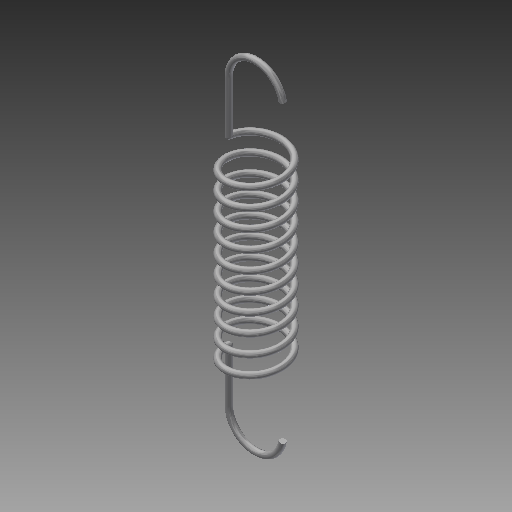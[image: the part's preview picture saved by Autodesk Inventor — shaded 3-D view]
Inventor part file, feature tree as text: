
AUTODESK INVENTOR PART (.ipt)
format: ipt  version: 2019 (Build 230136000, 136)  size: 1,031,168 bytes
history: native  units: mm
features: sketch x104, plane x32, other x32, extrude x10, sweep x6
ambient origin geometry x8: Origin, YZ Plane, XZ Plane, XY Plane, X Axis, Y Axis, Z Axis, Center Point
bodies: Solid1 (feature_tree)
feature tree (184):
  sketch  "Sketch1"  dims[d0=0.25mm d1=4.5mm]
  sketch  "3D Sketch2"
  plane  "Work PlaneSweep1"
  other  "First revolution with hook type 0(Right)"
  sketch  "Sketch8"  dims[d17=90.0deg d24=0.0mm d25=2.9972mm]
  plane  "Work PlaneExtrusion7"
  sketch  "Sketch10"  dims[d28=0.0mm d29=90.0deg d30=90.0deg d31=0.0mm d32=0.0mm d33=1.0mm]
  plane  "Work PlaneSweep2"
  sweep  "Sweep2"
  other  "Second revolution with hook type 0(Right)"
  sketch  "Sketch12"  dims[d38=90.0deg d54=10.0mm d55=10.0mm]
  plane  "Work PlaneExtrusion8"
  sketch  "Sketch110"  dims[d367=29.670597mm]
  sketch  "3D Sketch20"
  plane  "Work PlaneSweep3"
  sketch  "3D Sketch3"
  plane  "Work PlaneSweep6"
  other  "First revolution with hook type 0(Left)"
  sketch  "Sketch24"  dims[d180=90.0deg]
  plane  "Work PlaneExtrusion5"
  sketch  "Sketch18"  dims[d169=300.0deg d170=6.257mm]
  plane  "Work PlaneSweep7"
  sweep  "Sweep7"
  other  "Second revolution with hook type 0(Left)"
  sketch  "Sketch20"  dims[d173=300.0deg d174=6.257mm]
  plane  "Work PlaneExtrusion6"
  sketch  "Sketch22"  dims[d177=6.507mm d178=0.0mm]
  plane  "Work PlaneSweep8"
  other  "First revolution with hook type 1(Left)"
  sketch  "Sketch27"  dims[d182=6.507mm]
  plane  "Work PlaneExtrusion9"
  extrude  "Extrusion9"  TaperAngle=90.0deg  [1 undecoded]
  sketch  "Sketch29"  dims[d184=30.0mm d185=30.0mm d186=30.0mm]
  plane  "Work PlaneSweep9"
  other  "Second revolution with hook type 1(Left)"
  sketch  "Sketch32"  dims[d189=4.5mm]
  plane  "Work PlaneExtrusion10"
  sketch  "Sketch34"  dims[d191=300.0deg]
  sketch  "3D Sketch22"
  plane  "Work PlaneSweep10"
  other  "First revolution with hook type 1(Right)"
  sketch  "Sketch42"  dims[d195=40.0mm]
  plane  "Work PlaneExtrusion11"
  extrude  "Extrusion11"  Depth=2.9972mm TaperAngle=0.0deg
  sketch  "Sketch44"  dims[d197=0.0mm]
  plane  "Work PlaneSweep11"
  other  "Second revolution with hook type 1(Right)"
  sketch  "Sketch112"  dims[d373=20.0mm]
  plane  "Work PlaneExtrusion12"
  sketch  "Sketch114"  dims[d375=0.0mm]
  sketch  "3D Sketch24"
  plane  "Work PlaneSweep12"
  sketch  "Sketch46"  dims[d199=300.0deg]
  other  "First sweep with hook type 2(Left)"
  sweep  "SweepLeftHook21"
  sketch  "Sketch48"  dims[d200=6.257mm]
  other  "Second sweep with hook type 2(Left)"
  sweep  "SweepLeftHook22"
  sketch  "Sketch50"  dims[d201=0.0mm]
  other  "First sweep with hook type 2(Right)"
  sweep  "SweepRightHook21"
  sketch  "Sketch52"  dims[d202=90.0deg]
  other  "Second sweep with hook type 2(Right)"
  sweep  "SweepRightHook22"
  other  "First revolution with hook type 3(Left)"
  extrude  "Extrusion1"  Depth=20.0mm
  other  "Second revolution with hook type 3(Left)"
  extrude  "Extrusion2"  Depth=20.0mm
  sketch  "Sketch60"  dims[d209=90.0deg]
  plane  "Work PlaneSweep20"
  other  "First revolution with hook type 3(Right)"
  extrude  "Extrusion3"  Depth=20.0mm
  other  "Second revolution with hook type 3(Right)"
  extrude  "Extrusion4"  Depth=6.257mm
  sketch  "Sketch68"  dims[d216=40.0mm]
  plane  "Work Plane46"
  other  "First revolution with hook type 4(Left)"
  sketch  "Sketch71"  dims[d223=90.0deg]
  plane  "Work PlaneExtrusion13"
  extrude  "Extrusion13"  TaperAngle=90.0deg  [1 undecoded]
  sketch  "Sketch73"  dims[d229=90.0deg]
  plane  "Work PlaneSweep23"
  other  "Second revolution with hook type 4(Left)"
  sketch  "Sketch76"  dims[d238=50.0mm]
  plane  "Work PlaneExtrusion14"
  sketch  "Sketch78"  dims[d243=60.0mm]
  sketch  "3D Sketch26"
  plane  "Work PlaneSweep24"
  other  "First revolution with hook type 4(Right)"
  sketch  "Sketch86"  dims[d269=60.0mm]
  plane  "Work PlaneExtrusion15"
  extrude  "Extrusion15"  Depth=6.257mm
  sketch  "Sketch88"  dims[d282=60.0mm]
  plane  "Work PlaneSweep25"
  other  "Second revolution with hook type 4(Right)"
  sketch  "Sketch116"  dims[d377=210.0deg]
  plane  "Work PlaneExtrusion16"
  sketch  "Sketch118"  dims[d381=20.0mm]
  sketch  "3D Sketch28"
  plane  "Work PlaneSweep26"
  other  "First revolution with hook type 5(Left)"
  sketch  "Sketch91"  dims[d301=10.0mm d302=15.0mm d303=0.0mm d304=90.0deg d305=90.0deg d306=0.0mm d307=0.0mm]
  plane  "Work PlaneExtrusion17"
  extrude  "Extrusion17"  TaperAngle=300.0deg  [1 undecoded]
  other  "Second revolution with hook type 5(Left)"
  sketch  "Sketch95"  dims[d320=6.507mm]
  plane  "Work PlaneExtrusion18"
  other  "First revolution with hook type 5(Right)"
  sketch  "Sketch99"  dims[d331=1.5mm]
  plane  "Work PlaneExtrusion19"
  other  "Second revolution with hook type 5(Right)"
  sketch  "Sketch103"  dims[d364=8.514mm]
  plane  "Work PlaneExtrusion20"
  extrude  "Extrusion20"  TaperAngle=0.0deg  [1 undecoded]
  sketch  "Sketch105"  dims[d366=10.0mm]
  other  "First coil with hook type 6(Left)"
  other  "Second coil with hook type 6(Left)"
  other  "First coil with hook type 6(Right)"
  other  "Second coil with hook type 6(Right)"
  other  "Srf1"
  sketch  "Sketch3"  dims[d2=2.9972mm d3=10.0mm d4=100.0mm]
  sketch  "Sketch4"  dims[d5=0.0mm d6=90.0deg d7=90.0deg d8=0.0mm d9=0.0mm d12=1.0mm]
  sketch  "Sketch7"  dims[d13=0.0mm d14=90.0deg]
  other  "Srf2"
  sketch  "3D Sketch14"
  sketch  "Sketch16"  dims[d149=90.0deg d152=20.0mm]
  sketch  "Sketch26"  dims[d181=300.0deg]
  sketch  "Sketch31"  dims[d188=40.0mm]
  sketch  "Sketch36"  dims[d193=0.0mm]
  sketch  "Sketch41"  dims[d194=90.0deg]
  sketch  "Sketch54"  dims[d203=40.0mm]
  sketch  "Sketch55"  dims[d204=4.5mm d205=0.0mm]
  sketch  "Sketch56"  dims[d206=300.0deg]
  sketch  "Sketch58"  dims[d207=6.257mm]
  sketch  "Sketch59"  dims[d208=0.0mm]
  sketch  "Sketch61"  dims[d210=4.5mm]
  sketch  "Sketch62"  dims[d211=0.0mm]
  sketch  "Sketch63"  dims[d212=90.0deg]
  sketch  "Sketch64"  dims[d213=300.0deg]
  sketch  "Sketch66"  dims[d214=6.257mm]
  sketch  "Sketch67"  dims[d215=0.0mm]
  sketch  "Sketch69"  dims[d217=90.0deg]
  sketch  "Sketch70"  dims[d220=50.0mm]
  sketch  "Sketch75"  dims[d235=90.0deg]
  sketch  "Sketch80"  dims[d256=60.0mm]
  sketch  "Sketch85"  dims[d268=90.0deg]
  sketch  "Sketch90"  dims[d300=1.5mm]
  sketch  "Sketch94"  dims[d311=10.0mm d312=15.0mm d313=0.0mm d314=90.0deg d315=90.0deg d316=0.0mm d317=0.0mm d318=70.0mm d319=70.0mm]
  sketch  "Sketch98"  dims[d330=6.507mm]
  sketch  "Sketch102"  dims[d361=10.0mm]
  sketch  "Sketch13"  dims[d72=0.0mm d73=0.0mm d79=90.0deg]
  sketch  "Sketch111"  dims[d368=0.0mm]
  sketch  "Sketch33"  dims[d190=0.0mm]
  sketch  "Sketch35"  dims[d192=6.257mm]
  sketch  "Sketch113"  dims[d374=8.514mm]
  sketch  "Sketch115"  dims[d376=20.0mm]
  sketch  "Sketch77"  dims[d242=90.0deg]
  sketch  "Sketch79"  dims[d255=90.0deg]
  sketch  "Sketch117"  dims[d378=0.0mm]
  sketch  "Sketch119"  dims[d384=8.514mm d385=0.0mm d386=20.0mm d387=210.0deg d388=0.0mm d391=50.0mm d394=8.514mm d395=0.0mm d396=50.0mm d397=29.670597mm d398=0.0mm d401=50.0mm d404=8.514mm d405=0.0mm d406=50.0mm d407=29.670597mm d408=0.0mm d411=60.0mm d423=60.0mm d433=8.514mm d434=0.0mm d435=6.257mm d436=1.5mm d437=10.0mm d438=15.0mm d439=0.0mm d440=90.0deg d441=90.0deg d442=0.0mm d443=0.0mm d444=60.0mm d447=60.0mm d457=8.514mm d458=0.0mm d459=60.0mm d469=90.0deg d478=90.0deg d479=6.257mm d480=1.5mm d481=25.4mm d482=15.0mm d483=0.0mm d484=90.0deg d485=90.0deg d486=0.0mm d487=0.0mm d491=10.0mm d498=10.0mm d501=0.0mm d502=8.514mm d503=0.0mm d504=210.0deg d505=0.0mm d506=0.0mm d507=8.514mm d508=0.0mm d509=29.670597mm d510=0.0mm d511=10.0mm d512=0.0mm d513=8.514mm d514=0.0mm d515=29.670597mm d516=0.0mm d517=0.0mm d518=8.514mm d519=0.0mm d520=6.257mm d521=1.5mm d522=10.0mm d523=15.0mm d524=0.0mm d525=90.0deg d526=90.0deg d527=0.0mm d528=0.0mm d529=60.0mm d530=50.0mm d531=0.0mm d532=8.514mm d533=0.0mm d534=20.0mm d535=210.0deg d536=0.0mm d537=0.0mm d538=8.514mm d539=0.0mm d540=29.670597mm d541=0.0mm d542=50.0mm d543=0.0mm d544=8.514mm d545=0.0mm d546=60.0mm d547=6.257mm d548=1.5mm d549=10.0mm d550=15.0mm d551=0.0mm d552=90.0deg d553=90.0deg d554=0.0mm d555=0.0mm d561=10.0mm d564=0.0mm d565=8.514mm d566=0.0mm d567=10.0mm d569=29.670597mm d570=0.0mm d571=90.0deg d578=0.0mm d579=1.0mm d580=8.514mm d581=0.0mm d584=10.0mm d585=10.0mm d588=29.670597mm d589=0.0mm d590=0.0mm d591=0.0mm d592=0.0mm d593=0.0mm d594=0.0mm d595=0.0mm d596=0.0mm d597=0.0mm d598=0.0mm d599=0.0mm d600=0.0mm d601=0.0mm d602=0.0mm d603=0.0mm d604=0.0mm d605=0.0mm d606=0.0mm d607=0.0mm d608=0.0mm d609=0.0mm d610=0.0mm d611=0.0mm]
  sketch  "Sketch96"  dims[d321=1.5mm]
  sketch  "Sketch97"  dims[d322=10.0mm d323=15.0mm d324=0.0mm d325=90.0deg d326=90.0deg d327=0.0mm d328=0.0mm d329=70.0mm]
  sketch  "Sketch104"  dims[d365=0.0mm]
  sketch  "Sketch43"  dims[d196=4.5mm]
  sketch  "Sketch45"  dims[d198=90.0deg]
  sketch  "Sketch9"  dims[d26=10.0mm d27=100.0mm]
  sketch  "Sketch11"  dims[d34=0.0mm d36=0.0mm]
  sketch  "Sketch87"  dims[d281=90.0deg]
  sketch  "Sketch89"  dims[d299=6.507mm]
  sketch  "Sketch100"  dims[d332=10.0mm d333=15.0mm d334=0.0mm d335=90.0deg d336=90.0deg d337=0.0mm d338=0.0mm d339=70.0mm]
  sketch  "Sketch101"  dims[d350=10.0mm d352=10.0mm d353=10.0mm d356=10.0mm]
  sketch  "Sketch28"  dims[d183=0.0mm]
  sketch  "Sketch30"  dims[d187=90.0deg]
  sketch  "Sketch72"  dims[d226=50.0mm]
  sketch  "Sketch74"  dims[d232=50.0mm]
  sketch  "Sketch92"  dims[d308=6.507mm]
  sketch  "Sketch93"  dims[d310=1.5mm]
  sketch  "Sketch21"  dims[d175=0.0mm d176=300.0deg]
  sketch  "Sketch23"  dims[d179=30.0mm]
  sketch  "Sketch15"  dims[d86=90.0deg d87=20.0mm d90=20.0mm]
  sketch  "Sketch17"  dims[d155=90.0deg d156=20.0mm]
  sketch  "Sketch19"  dims[d171=0.0mm d172=90.0deg]
  other  "Base Coil(Right)"
  other  "Base Coil(Left)"
note: 4 required parameter values undecoded (feature->parameter linkage not recoverable at this tier; creation-order binding heuristic only, values carry confidence <= 0.55)
